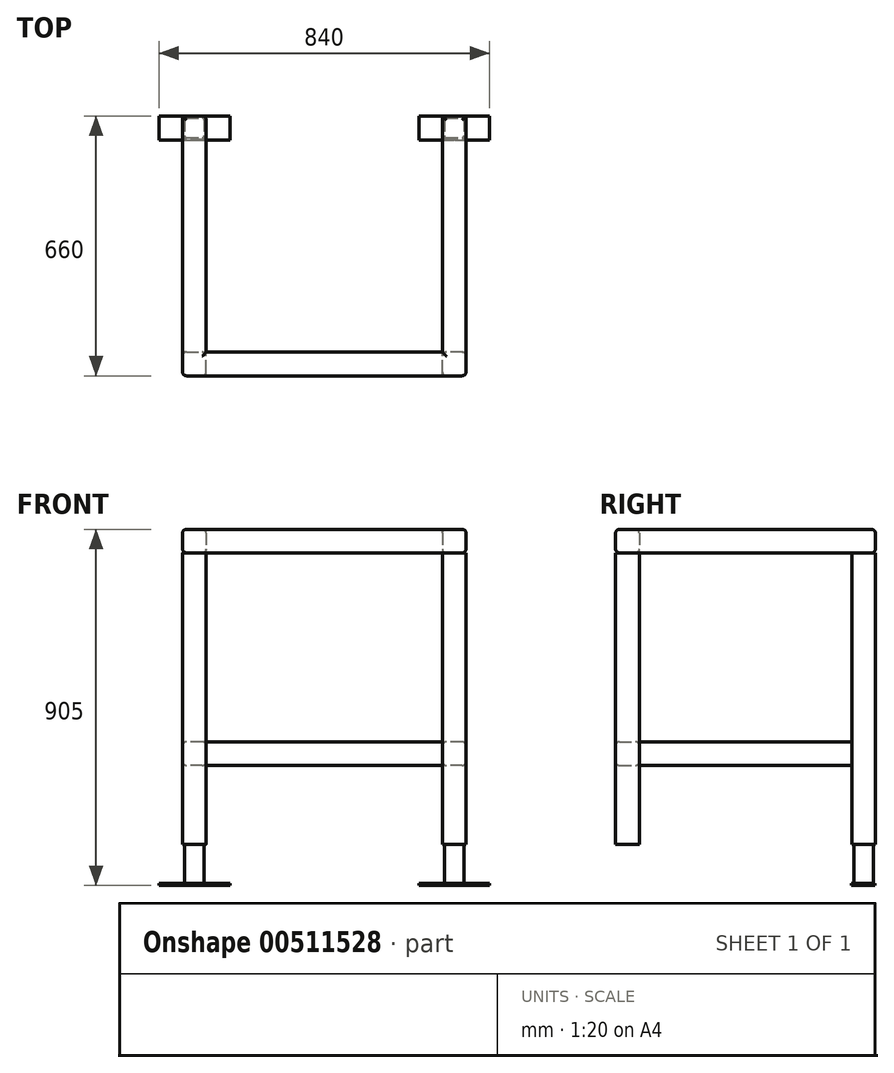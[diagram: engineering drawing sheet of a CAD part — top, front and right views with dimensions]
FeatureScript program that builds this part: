
annotation { "Feature Type Name" : "Feature", "Feature Type Description" : "" }
export const myFeature = defineFeature(function(context is Context, id is Id, definition is map)
    precondition{}
    {
        {
            var Q0;
            Q0=qCreatedBy(makeId("Top.planeOp"),FACE);
            var sketch = newSketch(context, id + "F0", { "sketchPlane" : qUnion([Q0])});
            skLineSegment(sketch, "E0.bottom", {"start": v(-477.97, 4.36) * mm, "end": v(-297.97, 4.36) * mm});
            skLineSegment(sketch, "E0.top", {"start": v(-477.97, -55.64) * mm, "end": v(-297.97, -55.64) * mm});
            skLineSegment(sketch, "E0.left", {"start": v(-477.97, 4.36) * mm, "end": v(-477.97, -55.64) * mm});
            skLineSegment(sketch, "E0.right", {"start": v(-297.97, 4.36) * mm, "end": v(-297.97, -55.64) * mm});
            skLineSegment(sketch, "E1.bottom", {"start": v(182.03, 4.36) * mm, "end": v(362.03, 4.36) * mm});
            skLineSegment(sketch, "E1.top", {"start": v(182.03, -55.64) * mm, "end": v(362.03, -55.64) * mm});
            skLineSegment(sketch, "E1.left", {"start": v(182.03, 4.36) * mm, "end": v(182.03, -55.64) * mm});
            skLineSegment(sketch, "E1.right", {"start": v(362.03, 4.36) * mm, "end": v(362.03, -55.64) * mm});
            skSolve(sketch);
        }
        {
            var Q0;
            Q0 = qSketchRegion(id + "F0", true);
            extrude(context, id + "F1", {"entities" : qUnion([Q0]), "depth" : 5 * mm});
        }
        {
            var Q0;
            Q0=makeQuery(id+"F1.opExtrude","CAP_FACE",FACE,{"disambiguationData":[OSD([sQuery(id+"F0.wireOp",EDGE,"E0.bottom"),sQuery(id+"F0.wireOp",EDGE,"E0.top"),sQuery(id+"F0.wireOp",EDGE,"E0.left"),sQuery(id+"F0.wireOp",EDGE,"E0.right")])],"isStart":false});
            var sketch = newSketch(context, id + "F2", { "sketchPlane" : qUnion([Q0])});
            skLineSegment(sketch, "E2.bottom", {"start": v(-412.97, 0) * mm, "end": v(-362.97, 0) * mm});
            skLineSegment(sketch, "E2.top", {"start": v(-412.97, -50) * mm, "end": v(-362.97, -50) * mm});
            skLineSegment(sketch, "E2.left", {"start": v(-412.97, 0) * mm, "end": v(-412.97, -50) * mm});
            skLineSegment(sketch, "E2.right", {"start": v(-362.97, 0) * mm, "end": v(-362.97, -50) * mm});
            skLineSegment(sketch, "E3.bottom", {"start": v(247.03, 0) * mm, "end": v(297.03, 0) * mm});
            skLineSegment(sketch, "E3.top", {"start": v(247.03, -50) * mm, "end": v(297.03, -50) * mm});
            skLineSegment(sketch, "E3.left", {"start": v(247.03, 0) * mm, "end": v(247.03, -50) * mm});
            skLineSegment(sketch, "E3.right", {"start": v(297.03, 0) * mm, "end": v(297.03, -50) * mm});
            skSolve(sketch);
        }
        {
            var Q0;
            Q0=makeQuery(id+"F2.imprint","IMPRINT",FACE,{"disambiguationData":[TD([[makeQuery(id+"F2.imprint","IMPRINT",EDGE,{"derivedFrom":sQuery(id+"F2.wireOp",EDGE,"E2.bottom")}),-1.0]])]});
            var Q1;
            Q1=makeQuery(id+"F2.imprint","IMPRINT",FACE,{"disambiguationData":[TD([[makeQuery(id+"F2.imprint","IMPRINT",EDGE,{"derivedFrom":sQuery(id+"F2.wireOp",EDGE,"E3.bottom")}),-1.0]])]});
            extrude(context, id + "F3", {"entities" : qUnion([Q0, Q1]), "depth" : 100 * mm});
        }
        {
            var Q0;
            Q0=makeQuery(id+"F3.opExtrude","SWEPT_EDGE",EDGE,{"disambiguationData":[OSD([sQuery(id+"F2.wireOp",EDGE,"E2.top"),sQuery(id+"F2.wireOp",EDGE,"E2.left")])]});
            var Q1;
            Q1=makeQuery(id+"F3.opExtrude","SWEPT_EDGE",EDGE,{"disambiguationData":[OSD([sQuery(id+"F2.wireOp",EDGE,"E2.top"),sQuery(id+"F2.wireOp",EDGE,"E2.right")])]});
            var Q2;
            Q2=makeQuery(id+"F3.opExtrude","SWEPT_EDGE",EDGE,{"disambiguationData":[OSD([sQuery(id+"F2.wireOp",EDGE,"E2.bottom"),sQuery(id+"F2.wireOp",EDGE,"E2.left")])]});
            var Q3;
            Q3=makeQuery(id+"F3.opExtrude","SWEPT_EDGE",EDGE,{"disambiguationData":[OSD([sQuery(id+"F2.wireOp",EDGE,"E2.bottom"),sQuery(id+"F2.wireOp",EDGE,"E2.right")])]});
            var Q4;
            Q4=makeQuery(id+"F3.opExtrude","SWEPT_EDGE",EDGE,{"disambiguationData":[OSD([sQuery(id+"F2.wireOp",EDGE,"E3.bottom"),sQuery(id+"F2.wireOp",EDGE,"E3.right")])]});
            var Q5;
            Q5=makeQuery(id+"F3.opExtrude","SWEPT_EDGE",EDGE,{"disambiguationData":[OSD([sQuery(id+"F2.wireOp",EDGE,"E3.bottom"),sQuery(id+"F2.wireOp",EDGE,"E3.left")])]});
            var Q6;
            Q6=makeQuery(id+"F3.opExtrude","SWEPT_EDGE",EDGE,{"disambiguationData":[OSD([sQuery(id+"F2.wireOp",EDGE,"E3.top"),sQuery(id+"F2.wireOp",EDGE,"E3.right")])]});
            var Q7;
            Q7=makeQuery(id+"F3.opExtrude","SWEPT_EDGE",EDGE,{"disambiguationData":[OSD([sQuery(id+"F2.wireOp",EDGE,"E3.top"),sQuery(id+"F2.wireOp",EDGE,"E3.left")])]});
            fillet(context, id + "F4", {"entities" : qUnion([Q0, Q1, Q2, Q3, Q4, Q5, Q6, Q7]), "radius" : 5 * mm, "tangentPropagation" : true, "allowEdgeOverflow" : false});
        }
        {
            var Q0;
            Q0=makeQuery(id+"F3.opExtrude","CAP_FACE",FACE,{"disambiguationData":[OSD([sQuery(id+"F2.wireOp",EDGE,"E2.bottom"),sQuery(id+"F2.wireOp",EDGE,"E2.top"),sQuery(id+"F2.wireOp",EDGE,"E2.left"),sQuery(id+"F2.wireOp",EDGE,"E2.right")])],"isStart":false});
            var sketch = newSketch(context, id + "F5", { "sketchPlane" : qUnion([Q0])});
            skArc(sketch, "E4.0", {"start": v(-407.97, 5) * mm, "mid": v(-415.04, 2.07) * mm, "end": v(-417.97, -5) * mm});
            skLineSegment(sketch, "E4.1", {"start": v(-367.97, 5) * mm, "end": v(-407.97, 5) * mm});
            skLineSegment(sketch, "E4.2", {"start": v(-417.97, -5) * mm, "end": v(-417.97, -45) * mm});
            skArc(sketch, "E4.3", {"start": v(-357.97, -5) * mm, "mid": v(-360.9, 2.07) * mm, "end": v(-367.97, 5) * mm});
            skArc(sketch, "E4.4", {"start": v(-417.97, -45) * mm, "mid": v(-415.04, -52.07) * mm, "end": v(-407.97, -55) * mm});
            skLineSegment(sketch, "E4.5", {"start": v(-407.97, -55) * mm, "end": v(-367.97, -55) * mm});
            skArc(sketch, "E4.6", {"start": v(-367.97, -55) * mm, "mid": v(-360.9, -52.07) * mm, "end": v(-357.97, -45) * mm});
            skLineSegment(sketch, "E4.7", {"start": v(-357.97, -45) * mm, "end": v(-357.97, -5) * mm});
            skArc(sketch, "E5.0", {"start": v(252.03, 5) * mm, "mid": v(244.96, 2.07) * mm, "end": v(242.03, -5) * mm});
            skLineSegment(sketch, "E5.1", {"start": v(292.03, 5) * mm, "end": v(252.03, 5) * mm});
            skLineSegment(sketch, "E5.2", {"start": v(242.03, -5) * mm, "end": v(242.03, -45) * mm});
            skArc(sketch, "E5.3", {"start": v(302.03, -5) * mm, "mid": v(299.1, 2.07) * mm, "end": v(292.03, 5) * mm});
            skArc(sketch, "E5.4", {"start": v(242.03, -45) * mm, "mid": v(244.96, -52.07) * mm, "end": v(252.03, -55) * mm});
            skLineSegment(sketch, "E5.5", {"start": v(252.03, -55) * mm, "end": v(292.03, -55) * mm});
            skArc(sketch, "E5.6", {"start": v(292.03, -55) * mm, "mid": v(299.1, -52.07) * mm, "end": v(302.03, -45) * mm});
            skLineSegment(sketch, "E5.7", {"start": v(302.03, -45) * mm, "end": v(302.03, -5) * mm});
            skLineSegment(sketch, "E6.bottom", {"start": v(-407.97, -655) * mm, "end": v(-367.97, -655) * mm});
            skLineSegment(sketch, "E6.top", {"start": v(-407.97, -595) * mm, "end": v(-367.97, -595) * mm});
            skLineSegment(sketch, "E6.left", {"start": v(-417.97, -645) * mm, "end": v(-417.97, -605) * mm});
            skLineSegment(sketch, "E6.right", {"start": v(-357.97, -645) * mm, "end": v(-357.97, -605) * mm});
            skLineSegment(sketch, "E7.bottom", {"start": v(252.03, -655) * mm, "end": v(292.03, -655) * mm});
            skLineSegment(sketch, "E7.top", {"start": v(252.03, -595) * mm, "end": v(292.03, -595) * mm});
            skLineSegment(sketch, "E7.left", {"start": v(242.03, -645) * mm, "end": v(242.03, -605) * mm});
            skLineSegment(sketch, "E7.right", {"start": v(302.03, -645) * mm, "end": v(302.03, -605) * mm});
            skPoint(sketch, "E8.visualSharp", {"position": v(-417.97, -595) * mm});
            skArc(sketch, "E8.filletArc", {"start": v(-407.97, -595) * mm, "mid": v(-415.04, -597.93) * mm, "end": v(-417.97, -605) * mm});
            skPoint(sketch, "E9.visualSharp", {"position": v(-357.97, -595) * mm});
            skArc(sketch, "E9.filletArc", {"start": v(-357.97, -605) * mm, "mid": v(-360.9, -597.93) * mm, "end": v(-367.97, -595) * mm});
            skPoint(sketch, "E10.visualSharp", {"position": v(-357.97, -655) * mm});
            skArc(sketch, "E10.filletArc", {"start": v(-367.97, -655) * mm, "mid": v(-360.9, -652.07) * mm, "end": v(-357.97, -645) * mm});
            skPoint(sketch, "E11.visualSharp", {"position": v(-417.97, -655) * mm});
            skArc(sketch, "E11.filletArc", {"start": v(-417.97, -645) * mm, "mid": v(-415.04, -652.07) * mm, "end": v(-407.97, -655) * mm});
            skPoint(sketch, "E12.visualSharp", {"position": v(242.03, -595) * mm});
            skArc(sketch, "E12.filletArc", {"start": v(252.03, -595) * mm, "mid": v(244.96, -597.93) * mm, "end": v(242.03, -605) * mm});
            skPoint(sketch, "E13.visualSharp", {"position": v(242.03, -655) * mm});
            skArc(sketch, "E13.filletArc", {"start": v(242.03, -645) * mm, "mid": v(244.96, -652.07) * mm, "end": v(252.03, -655) * mm});
            skPoint(sketch, "E14.visualSharp", {"position": v(302.03, -655) * mm});
            skArc(sketch, "E14.filletArc", {"start": v(292.03, -655) * mm, "mid": v(299.1, -652.07) * mm, "end": v(302.03, -645) * mm});
            skPoint(sketch, "E15.visualSharp", {"position": v(302.03, -595) * mm});
            skArc(sketch, "E15.filletArc", {"start": v(302.03, -605) * mm, "mid": v(299.1, -597.93) * mm, "end": v(292.03, -595) * mm});
            skSolve(sketch);
        }
        {
            var Q0;
            Q0=makeQuery(id+"F5.imprint","IMPRINT",FACE,{"disambiguationData":[TD([[makeQuery(id+"F5.imprint","IMPRINT",EDGE,{"derivedFrom":sQuery(id+"F5.wireOp",EDGE,"E4.0")}),1.0]])]});
            var Q1;
            {var subQ3=sQuery(id+"F2.wireOp",EDGE,"E2.bottom");Q1=makeQuery(id+"F5.imprint","IMPRINT",FACE,{"disambiguationData":[TD([[makeQuery(id+"F5.imprint","IMPRINT",EDGE,{"derivedFrom":makeQuery(id+"F3.opExtrude","CAP_EDGE",EDGE,{"disambiguationData":[OSD([subQ3])],"isStart":false})}),-1.0]])]});}
            var Q2;
            Q2=makeQuery(id+"F5.imprint","IMPRINT",FACE,{"disambiguationData":[TD([[makeQuery(id+"F5.imprint","IMPRINT",EDGE,{"derivedFrom":sQuery(id+"F5.wireOp",EDGE,"E5.0")}),1.0]])]});
            var Q3;
            Q3=makeQuery(id+"F5.imprint","IMPRINT",FACE,{"disambiguationData":[TD([[makeQuery(id+"F5.imprint","IMPRINT",EDGE,{"derivedFrom":sQuery(id+"F5.wireOp",EDGE,"E7.bottom")}),1.0]])]});
            var Q4;
            Q4=makeQuery(id+"F5.imprint","IMPRINT",FACE,{"disambiguationData":[TD([[makeQuery(id+"F5.imprint","IMPRINT",EDGE,{"derivedFrom":sQuery(id+"F5.wireOp",EDGE,"E6.bottom")}),1.0]])]});
            extrude(context, id + "F6", {"entities" : qUnion([Q0, Q1, Q2, Q3, Q4]), "depth" : 740 * mm});
        }
        {
            var Q0;
            Q0=makeQuery(id+"F6.opExtrude","CAP_FACE",FACE,{"disambiguationData":[OSD([sQuery(id+"F5.wireOp",EDGE,"E4.0"),sQuery(id+"F5.wireOp",EDGE,"E4.1"),sQuery(id+"F5.wireOp",EDGE,"E4.2"),sQuery(id+"F5.wireOp",EDGE,"E4.3"),sQuery(id+"F5.wireOp",EDGE,"E4.4"),sQuery(id+"F5.wireOp",EDGE,"E4.5"),sQuery(id+"F5.wireOp",EDGE,"E4.6"),sQuery(id+"F5.wireOp",EDGE,"E4.7")])],"isStart":false});
            var sketch = newSketch(context, id + "F7", { "sketchPlane" : qUnion([Q0])});
            skLineSegment(sketch, "E16.bottom", {"start": v(-417.97, 5) * mm, "end": v(-357.97, 5) * mm});
            skLineSegment(sketch, "E16.top", {"start": v(-417.97, -655) * mm, "end": v(302.03, -655) * mm});
            skLineSegment(sketch, "E16.left", {"start": v(-417.97, 5) * mm, "end": v(-417.97, -655) * mm});
            skLineSegment(sketch, "E16.right", {"start": v(302.03, 5) * mm, "end": v(302.03, -655) * mm});
            skLineSegment(sketch, "E17.top", {"start": v(-357.97, -595) * mm, "end": v(242.03, -595) * mm});
            skLineSegment(sketch, "E17.left", {"start": v(-357.97, -55) * mm, "end": v(-357.97, -595) * mm});
            skLineSegment(sketch, "E17.right", {"start": v(242.03, -55) * mm, "end": v(242.03, -595) * mm});
            skLineSegment(sketch, "E18", {"start": v(242.03, -55) * mm, "end": v(242.03, 5) * mm});
            skLineSegment(sketch, "E19", {"start": v(-357.97, -55) * mm, "end": v(-357.97, 5) * mm});
            skLineSegment(sketch, "E20.trimOffspring", {"start": v(242.03, 5) * mm, "end": v(302.03, 5) * mm});
            skSolve(sketch);
        }
        {
            var Q0;
            Q0 = qSketchRegion(id + "F7", true);
            extrude(context, id + "F8", {"entities" : qUnion([Q0]), "depth" : 60 * mm});
        }
        {
            var Q0;
            Q0=makeQuery(id+"F8.opExtrude","CAP_FACE",FACE,{"disambiguationData":[OSD([sQuery(id+"F7.wireOp",EDGE,"E16.bottom"),sQuery(id+"F7.wireOp",EDGE,"E16.top"),sQuery(id+"F7.wireOp",EDGE,"E16.left"),sQuery(id+"F7.wireOp",EDGE,"E16.right"),sQuery(id+"F7.wireOp",EDGE,"E17.top"),sQuery(id+"F7.wireOp",EDGE,"E17.left"),sQuery(id+"F7.wireOp",EDGE,"E17.right"),sQuery(id+"F7.wireOp",EDGE,"E18"),sQuery(id+"F7.wireOp",EDGE,"E19"),sQuery(id+"F7.wireOp",EDGE,"E20.trimOffspring")])],"isStart":false});
            var Q1;
            Q1=makeQuery(id+"F8.opExtrude","SWEPT_EDGE",EDGE,{"disambiguationData":[OSD([sQuery(id+"F7.wireOp",EDGE,"E16.top"),sQuery(id+"F7.wireOp",EDGE,"E16.left")])]});
            var Q2;
            Q2=makeQuery(id+"F8.opExtrude","SWEPT_EDGE",EDGE,{"disambiguationData":[OSD([sQuery(id+"F7.wireOp",EDGE,"E16.top"),sQuery(id+"F7.wireOp",EDGE,"E16.right")])]});
            var Q3;
            Q3=makeQuery(id+"F8.opExtrude","SWEPT_EDGE",EDGE,{"disambiguationData":[OSD([sQuery(id+"F7.wireOp",EDGE,"E16.bottom"),sQuery(id+"F7.wireOp",EDGE,"E19")])]});
            var Q4;
            Q4=makeQuery(id+"F8.opExtrude","CAP_FACE",FACE,{"disambiguationData":[OSD([sQuery(id+"F7.wireOp",EDGE,"E16.bottom"),sQuery(id+"F7.wireOp",EDGE,"E16.top"),sQuery(id+"F7.wireOp",EDGE,"E16.left"),sQuery(id+"F7.wireOp",EDGE,"E16.right"),sQuery(id+"F7.wireOp",EDGE,"E17.top"),sQuery(id+"F7.wireOp",EDGE,"E17.left"),sQuery(id+"F7.wireOp",EDGE,"E17.right"),sQuery(id+"F7.wireOp",EDGE,"E18"),sQuery(id+"F7.wireOp",EDGE,"E19"),sQuery(id+"F7.wireOp",EDGE,"E20.trimOffspring")])],"isStart":true});
            fillet(context, id + "F9", {"entities" : qUnion([Q0, Q1, Q2, Q3, Q4]), "radius" : 10 * mm, "tangentPropagation" : true, "allowEdgeOverflow" : false});
        }
        {
            var Q0;
            Q0=makeQuery(id+"F6.opExtrude","SWEPT_FACE",FACE,{"disambiguationData":[OSD([sQuery(id+"F5.wireOp",EDGE,"E6.right")])]});
            var sketch = newSketch(context, id + "F10", { "sketchPlane" : qUnion([Q0])});
            skLineSegment(sketch, "E21.bottom", {"start": v(-645, 305) * mm, "end": v(-605, 305) * mm});
            skLineSegment(sketch, "E21.top", {"start": v(-645, 365) * mm, "end": v(-605, 365) * mm});
            skLineSegment(sketch, "E21.left", {"start": v(-655, 315) * mm, "end": v(-655, 355) * mm});
            skLineSegment(sketch, "E21.right", {"start": v(-595, 315) * mm, "end": v(-595, 355) * mm});
            skPoint(sketch, "E22.visualSharp", {"position": v(-655, 365) * mm});
            skArc(sketch, "E22.filletArc", {"start": v(-645, 365) * mm, "mid": v(-652.07, 362.07) * mm, "end": v(-655, 355) * mm});
            skPoint(sketch, "E23.visualSharp", {"position": v(-595, 365) * mm});
            skArc(sketch, "E23.filletArc", {"start": v(-595, 355) * mm, "mid": v(-597.93, 362.07) * mm, "end": v(-605, 365) * mm});
            skPoint(sketch, "E24.visualSharp", {"position": v(-595, 305) * mm});
            skArc(sketch, "E24.filletArc", {"start": v(-605, 305) * mm, "mid": v(-597.93, 307.93) * mm, "end": v(-595, 315) * mm});
            skPoint(sketch, "E25.visualSharp", {"position": v(-655, 305) * mm});
            skArc(sketch, "E25.filletArc", {"start": v(-655, 315) * mm, "mid": v(-652.07, 307.93) * mm, "end": v(-645, 305) * mm});
            skSolve(sketch);
        }
        {
            var Q0;
            Q0 = qSketchRegion(id + "F10", true);
            extrude(context, id + "F11", {"entities" : qUnion([Q0]), "depth" : 600 * mm});
        }
        {
            var Q0;
            Q0=makeQuery(id+"F6.opExtrude","SWEPT_FACE",FACE,{"disambiguationData":[OSD([sQuery(id+"F5.wireOp",EDGE,"E5.5")])]});
            var sketch = newSketch(context, id + "F12", { "sketchPlane" : qUnion([Q0])});
            skLineSegment(sketch, "E26.bottom", {"start": v(292.03, 305) * mm, "end": v(252.03, 305) * mm});
            skLineSegment(sketch, "E26.top", {"start": v(292.03, 365) * mm, "end": v(252.03, 365) * mm});
            skLineSegment(sketch, "E26.left", {"start": v(302.03, 315) * mm, "end": v(302.03, 355) * mm});
            skLineSegment(sketch, "E26.right", {"start": v(242.03, 315) * mm, "end": v(242.03, 355) * mm});
            skLineSegment(sketch, "E27.1.0.0", {"start": v(-367.97, 365) * mm, "end": v(-407.97, 365) * mm});
            skLineSegment(sketch, "E27.1.0.1", {"start": v(-417.97, 315) * mm, "end": v(-417.97, 355) * mm});
            skLineSegment(sketch, "E27.1.0.2", {"start": v(-367.97, 305) * mm, "end": v(-407.97, 305) * mm});
            skLineSegment(sketch, "E27.1.0.3", {"start": v(-357.97, 315) * mm, "end": v(-357.97, 355) * mm});
            skLineSegment(sketch, "E27.2.0.0", {"start": v(-1017.97, 365) * mm, "end": v(-1077.97, 365) * mm});
            skLineSegment(sketch, "E27.2.0.1", {"start": v(-1077.97, 305) * mm, "end": v(-1077.97, 365) * mm});
            skLineSegment(sketch, "E27.2.0.2", {"start": v(-1017.97, 305) * mm, "end": v(-1077.97, 305) * mm});
            skLineSegment(sketch, "E27.2.0.3", {"start": v(-1017.97, 305) * mm, "end": v(-1017.97, 365) * mm});
            skLineSegment(sketch, "E27.direction1", {"start": v(242.03, 365) * mm, "end": v(-417.97, 365) * mm, "construction": true});
            skPoint(sketch, "E28.visualSharp", {"position": v(-357.97, 365) * mm});
            skArc(sketch, "E28.filletArc", {"start": v(-357.97, 355) * mm, "mid": v(-360.9, 362.07) * mm, "end": v(-367.97, 365) * mm});
            skPoint(sketch, "E29.visualSharp", {"position": v(-417.97, 305) * mm});
            skArc(sketch, "E29.filletArc", {"start": v(-417.97, 315) * mm, "mid": v(-415.04, 307.93) * mm, "end": v(-407.97, 305) * mm});
            skPoint(sketch, "E30.visualSharp", {"position": v(-357.97, 305) * mm});
            skArc(sketch, "E30.filletArc", {"start": v(-367.97, 305) * mm, "mid": v(-360.9, 307.93) * mm, "end": v(-357.97, 315) * mm});
            skPoint(sketch, "E31.visualSharp", {"position": v(-417.97, 365) * mm});
            skArc(sketch, "E31.filletArc", {"start": v(-407.97, 365) * mm, "mid": v(-415.04, 362.07) * mm, "end": v(-417.97, 355) * mm});
            skPoint(sketch, "E32.visualSharp", {"position": v(242.03, 305) * mm});
            skArc(sketch, "E32.filletArc", {"start": v(242.03, 315) * mm, "mid": v(244.96, 307.93) * mm, "end": v(252.03, 305) * mm});
            skPoint(sketch, "E33.visualSharp", {"position": v(242.03, 365) * mm});
            skArc(sketch, "E33.filletArc", {"start": v(252.03, 365) * mm, "mid": v(244.96, 362.07) * mm, "end": v(242.03, 355) * mm});
            skPoint(sketch, "E34.visualSharp", {"position": v(302.03, 365) * mm});
            skArc(sketch, "E34.filletArc", {"start": v(302.03, 355) * mm, "mid": v(299.1, 362.07) * mm, "end": v(292.03, 365) * mm});
            skPoint(sketch, "E35.visualSharp", {"position": v(302.03, 305) * mm});
            skArc(sketch, "E35.filletArc", {"start": v(292.03, 305) * mm, "mid": v(299.1, 307.93) * mm, "end": v(302.03, 315) * mm});
            skSolve(sketch);
        }
        {
            var Q0;
            Q0=makeQuery(id+"F12.imprint","IMPRINT",FACE,{"disambiguationData":[TD([[makeQuery(id+"F12.imprint","IMPRINT",EDGE,{"derivedFrom":sQuery(id+"F12.wireOp",EDGE,"E27.1.0.0")}),1.0]])]});
            var Q1;
            Q1=makeQuery(id+"F12.imprint","IMPRINT",FACE,{"disambiguationData":[TD([[makeQuery(id+"F12.imprint","IMPRINT",EDGE,{"derivedFrom":sQuery(id+"F12.wireOp",EDGE,"E26.right")}),-1.0]])]});
            var Q2;
            {var subQ0=sQuery(id+"F12.wireOp",EDGE,"E26.bottom");Q2=makeQuery(id+"F12.imprint","IMPRINT",FACE,{"disambiguationData":[TD([[makeQuery(id+"F12.imprint","IMPRINT",EDGE,{"derivedFrom":subQ0}),-1.0]])]});}
            var Q3;
            Q3=makeQuery(id+"F12.imprint","IMPRINT",FACE,{"disambiguationData":[TD([[makeQuery(id+"F12.imprint","IMPRINT",EDGE,{"derivedFrom":sQuery(id+"F12.wireOp",EDGE,"E26.left")}),1.0]])]});
            extrude(context, id + "F13", {"entities" : qUnion([Q0, Q1, Q2, Q3]), "depth" : 540 * mm});
        }
    });
